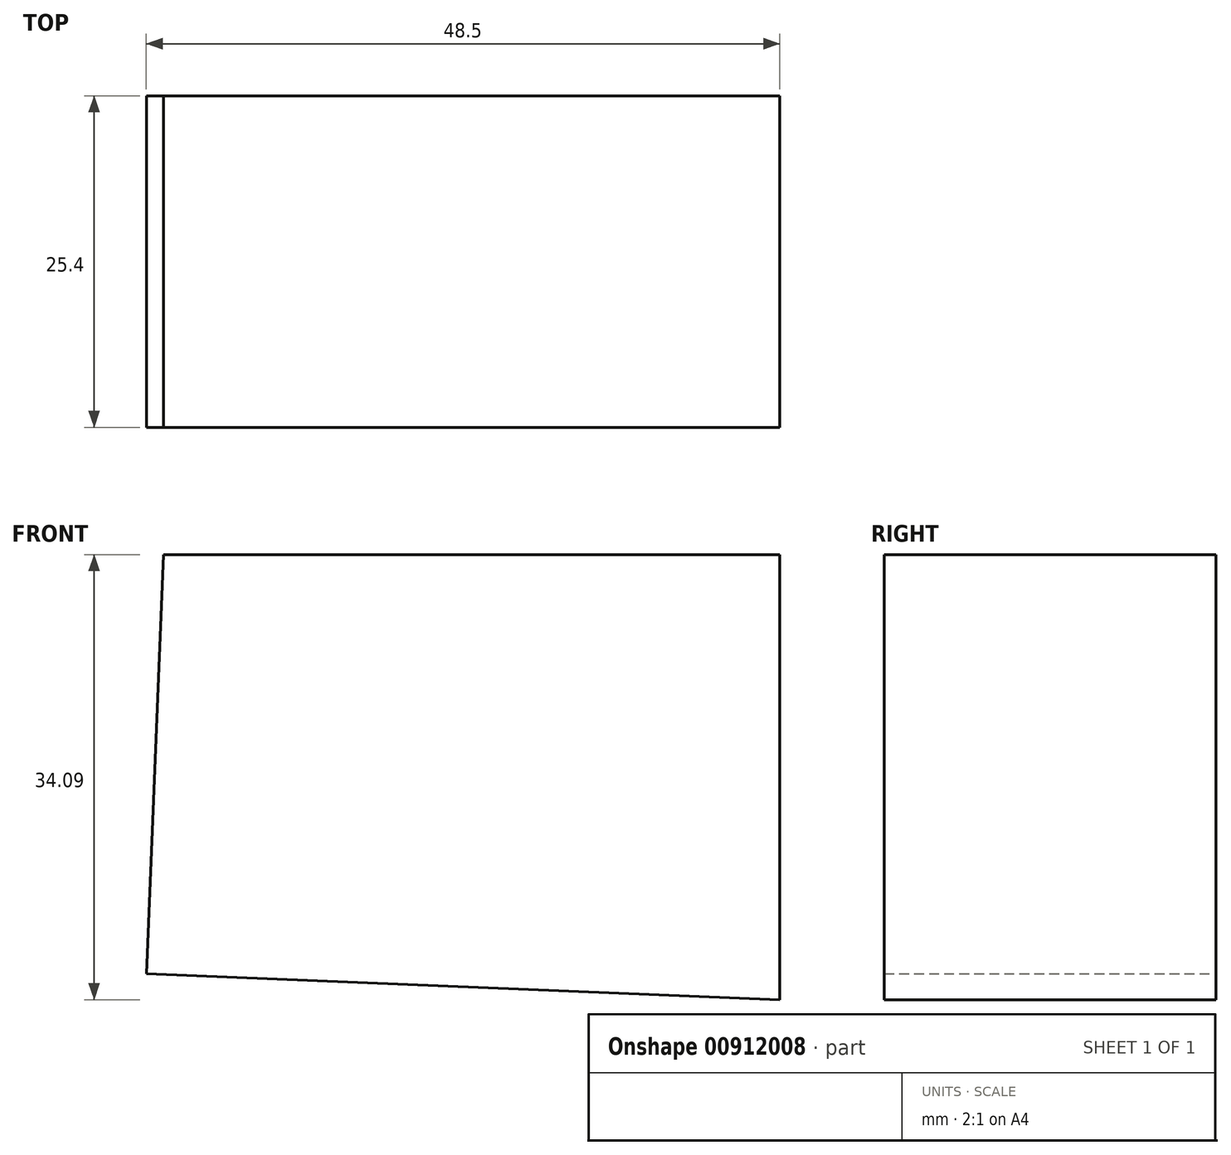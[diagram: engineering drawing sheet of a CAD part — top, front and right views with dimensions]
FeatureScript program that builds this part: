
annotation { "Feature Type Name" : "Feature", "Feature Type Description" : "" }
export const myFeature = defineFeature(function(context is Context, id is Id, definition is map)
    precondition{}
    {
        {
            var Q0;
            Q0=qCreatedBy(makeId("Front.planeOp"),FACE);
            var sketch = newSketch(context, id + "F0", { "sketchPlane" : qUnion([Q0])});
            skLineSegment(sketch, "E0", {"start": v(-59.82, 43.23) * mm, "end": v(-12.63, 43.23) * mm});
            skLineSegment(sketch, "E1", {"start": v(-12.63, 9.14) * mm, "end": v(-12.63, 43.23) * mm});
            skLineSegment(sketch, "E2", {"start": v(-61.13, 11.12) * mm, "end": v(-12.63, 9.14) * mm});
            skLineSegment(sketch, "E3", {"start": v(-59.82, 43.23) * mm, "end": v(-61.13, 11.12) * mm});
            skSolve(sketch);
        }
        {
            var Q0;
            Q0 = qSketchRegion(id + "F0", true);
            extrude(context, id + "F1", {"entities" : qUnion([Q0]), "depth" : 25.4 * mm, "offsetDistance" : 25.4 * mm});
        }
    });
